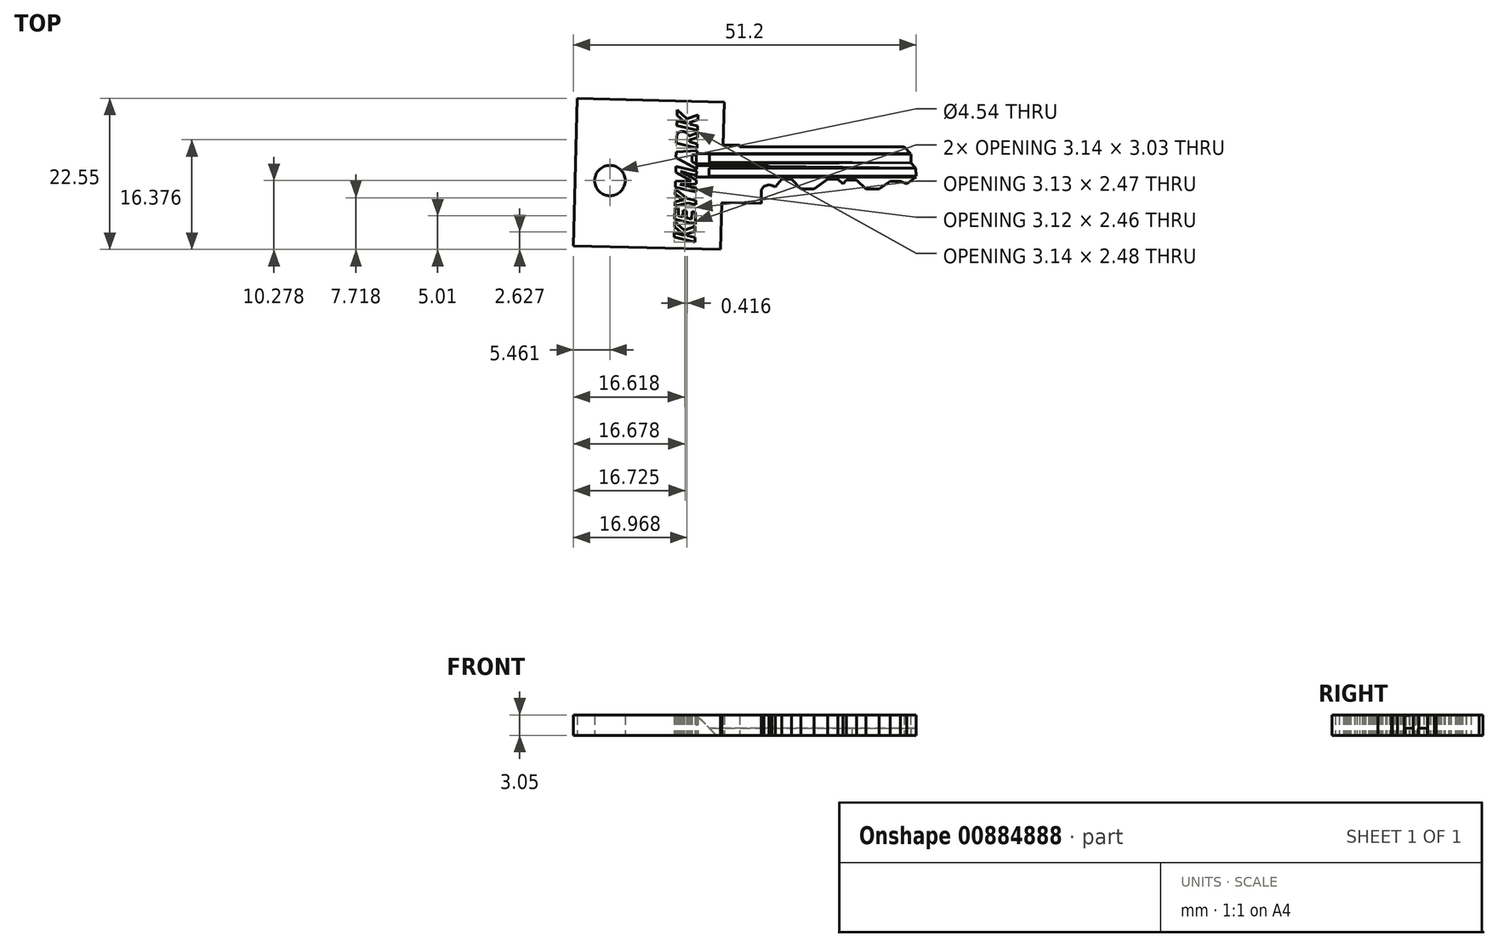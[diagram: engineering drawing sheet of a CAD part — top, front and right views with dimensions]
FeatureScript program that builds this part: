
annotation { "Feature Type Name" : "Feature", "Feature Type Description" : "" }
export const myFeature = defineFeature(function(context is Context, id is Id, definition is map)
    precondition{}
    {
        {
            var Q0;
            Q0=qCreatedBy(makeId("Top.planeOp"),FACE);
            var sketch = newSketch(context, id + "F0", { "sketchPlane" : qUnion([Q0])});
            skLineSegment(sketch, "E0", {"start": v(-36.72, -12.14) * mm, "end": v(-36.54, -5.12) * mm});
            skLineSegment(sketch, "E1", {"start": v(-36.72, -12.14) * mm, "end": v(-58.71, -11.59) * mm});
            skLineSegment(sketch, "E2", {"start": v(-58.16, 10.4) * mm, "end": v(-58.71, -11.59) * mm});
            skLineSegment(sketch, "E3", {"start": v(-36.17, 9.86) * mm, "end": v(-58.16, 10.4) * mm});
            skLineSegment(sketch, "E4", {"start": v(-36.54, -5.12) * mm, "end": v(-30.61, -5.27) * mm});
            skLineSegment(sketch, "E5", {"start": v(-30.61, -5.27) * mm, "end": v(-30.61, -3.25) * mm});
            skLineSegment(sketch, "E6", {"start": v(-28.53, -2.78) * mm, "end": v(-27.6, -1.64) * mm});
            skLineSegment(sketch, "E7", {"start": v(-27.6, -1.64) * mm, "end": v(-26.15, -1.64) * mm});
            skLineSegment(sketch, "E8", {"start": v(-26.15, -1.64) * mm, "end": v(-24.74, -3.13) * mm});
            skLineSegment(sketch, "E9", {"start": v(-24.74, -3.13) * mm, "end": v(-22.78, -3.13) * mm});
            skLineSegment(sketch, "E10", {"start": v(-22.78, -3.13) * mm, "end": v(-20.7, -1.64) * mm});
            skLineSegment(sketch, "E11", {"start": v(-20.7, -1.64) * mm, "end": v(-19.22, -1.64) * mm});
            skLineSegment(sketch, "E12", {"start": v(-19.22, -1.64) * mm, "end": v(-18.48, -2.35) * mm});
            skLineSegment(sketch, "E13", {"start": v(-18.48, -2.35) * mm, "end": v(-17.93, -1.77) * mm});
            skLineSegment(sketch, "E14", {"start": v(-17.93, -1.77) * mm, "end": v(-16.45, -1.77) * mm});
            skLineSegment(sketch, "E15", {"start": v(-16.45, -1.77) * mm, "end": v(-15.04, -3.13) * mm});
            skLineSegment(sketch, "E16", {"start": v(-15.04, -3.13) * mm, "end": v(-13.04, -3.13) * mm});
            skLineSegment(sketch, "E17", {"start": v(-13.04, -3.13) * mm, "end": v(-11.4, -1.95) * mm});
            skLineSegment(sketch, "E18", {"start": v(-11.4, -1.95) * mm, "end": v(-9.87, -1.95) * mm});
            skLineSegment(sketch, "E19", {"start": v(-9.87, -1.95) * mm, "end": v(-8.94, -2.35) * mm});
            skLineSegment(sketch, "E20", {"start": v(-8.94, -2.35) * mm, "end": v(-7.53, -1.34) * mm});
            skLineSegment(sketch, "E21", {"start": v(-7.57, 0) * mm, "end": v(-8.36, 0.85) * mm});
            skLineSegment(sketch, "E22", {"start": v(-8.36, 2.17) * mm, "end": v(-9.29, 3.17) * mm});
            skLineSegment(sketch, "E23", {"start": v(-9.29, 3.17) * mm, "end": v(-36.34, 3.17) * mm});
            skLineSegment(sketch, "E24.trimOffspring", {"start": v(-36.34, 3.17) * mm, "end": v(-36.17, 9.86) * mm});
            skLineSegment(sketch, "E25", {"start": v(-8.36, 2.17) * mm, "end": v(-37.36, 2.17) * mm});
            skLineSegment(sketch, "E26", {"start": v(-37.36, 2.17) * mm, "end": v(-37.36, 0.67) * mm});
            skLineSegment(sketch, "E27", {"start": v(-37.36, 0.67) * mm, "end": v(-8.36, 0.85) * mm});
            skLineSegment(sketch, "E28", {"start": v(-7.53, -1.34) * mm, "end": v(-37.42, -1.34) * mm});
            skLineSegment(sketch, "E29", {"start": v(-37.42, -1.34) * mm, "end": v(-37.42, 0.32) * mm});
            skLineSegment(sketch, "E30", {"start": v(-37.42, 0.32) * mm, "end": v(-7.57, 0) * mm});
            skLineSegment(sketch, "E31", {"start": v(-30.61, -3.25) * mm, "end": v(-30.26, -2.7) * mm});
            skLineSegment(sketch, "E32", {"start": v(-30.26, -2.7) * mm, "end": v(-29.5, -2.5) * mm});
            skLineSegment(sketch, "E33", {"start": v(-29.5, -2.5) * mm, "end": v(-29.08, -2.63) * mm});
            skLineSegment(sketch, "E34", {"start": v(-29.08, -2.63) * mm, "end": v(-28.53, -2.78) * mm});
            skLineSegment(sketch, "E35", {"start": v(-36.33, 3.42) * mm, "end": v(-33.86, 3.42) * mm});
            skLineSegment(sketch, "E36", {"start": v(-33.86, 3.42) * mm, "end": v(-33.86, 3.17) * mm});
            skText(sketch, "E37", { "text": "KEYMARK", "fontName": "OpenSans-BoldItalic.ttf"});
            const initialGuessF0  = {"E37": [-0.04058, -0.01114, 0.02492, 0.99969, 0.00313]};
            skSetInitialGuess(sketch, initialGuessF0);
            skSolve(sketch);
        }
        {
            var Q0;
            Q0=qCreatedBy(makeId("Top.planeOp"),FACE);
            var sketch = newSketch(context, id + "F1", { "sketchPlane" : qUnion([Q0])});
            skLineSegment(sketch, "E38", {"start": v(-7.51, -1.2) * mm, "end": v(-38.7, -1.2) * mm});
            skLineSegment(sketch, "E39", {"start": v(-38.62, 0) * mm, "end": v(-7.59, 0) * mm});
            skLineSegment(sketch, "E40", {"start": v(-8.3, 0.8) * mm, "end": v(-38.62, 0.8) * mm});
            skPoint(sketch, "E41", {"position": v(-8.3, 2.11) * mm});
            skLineSegment(sketch, "E42", {"start": v(-38.52, 2.11) * mm, "end": v(-8.3, 2.11) * mm});
            skLineSegment(sketch, "E43", {"start": v(-7.51, -1.2) * mm, "end": v(-7.59, 0) * mm});
            skLineSegment(sketch, "E44", {"start": v(-8.3, 2.11) * mm, "end": v(-8.3, 0.8) * mm});
            skLineSegment(sketch, "E45", {"start": v(-38.52, 2.11) * mm, "end": v(-38.62, 0.8) * mm});
            skLineSegment(sketch, "E46", {"start": v(-38.62, 0) * mm, "end": v(-38.7, -1.2) * mm});
            skSolve(sketch);
        }
        {
            var Q0;
            Q0 = qSketchRegion(id + "F0", true);
            extrude(context, id + "F2", {"entities" : qUnion([Q0]), "depth" : 3.05 * mm, "offsetDistance" : 25 * mm});
        }
        {
            var Q0;
            Q0 = qSketchRegion(id + "F1", true);
            extrude(context, id + "F3", {"entities" : qUnion([Q0]), "operationType" : NewBodyOperationType.ADD, "depth" : 1.06 * mm, "offsetDistance" : 25 * mm});
        }
        {
            var Q0;
            Q0=makeQuery(id+"F2.opExtrude","CAP_EDGE",EDGE,{"disambiguationData":[OSD([sQuery(id+"F0.wireOp",EDGE,"E26")])],"isStart":false});
            chamfer(context, id + "F4", {"entities" : qUnion([Q0]), "width" : 3 * mm, "tangentPropagation" : true});
        }
        {
            var Q0;
            Q0=makeQuery(id+"F2.opExtrude","CAP_EDGE",EDGE,{"disambiguationData":[OSD([sQuery(id+"F0.wireOp",EDGE,"E29")])],"isStart":false});
            chamfer(context, id + "F5", {"entities" : qUnion([Q0]), "width" : 3 * mm, "tangentPropagation" : true});
        }
        {
            var Q0;
            Q0=qCreatedBy(makeId("Top.planeOp"),FACE);
            var sketch = newSketch(context, id + "F6", { "sketchPlane" : qUnion([Q0])});
            skCircle(sketch, "E47", {"center": v(-53.25, -1.86) * mm, "radius": 2.27 * mm});
            skSolve(sketch);
        }
        {
            var Q0;
            Q0=makeQuery(id+"F6.imprint","IMPRINT",FACE,{"disambiguationData":[TD([[makeQuery(id+"F6.imprint","IMPRINT",EDGE,{"derivedFrom":sQuery(id+"F6.wireOp",EDGE,"E47")}),1.0]])]});
            extrude(context, id + "F7", {"entities" : qUnion([Q0]), "operationType" : NewBodyOperationType.REMOVE, "depth" : 8.9 * mm, "offsetDistance" : 25 * mm});
        }
    });
